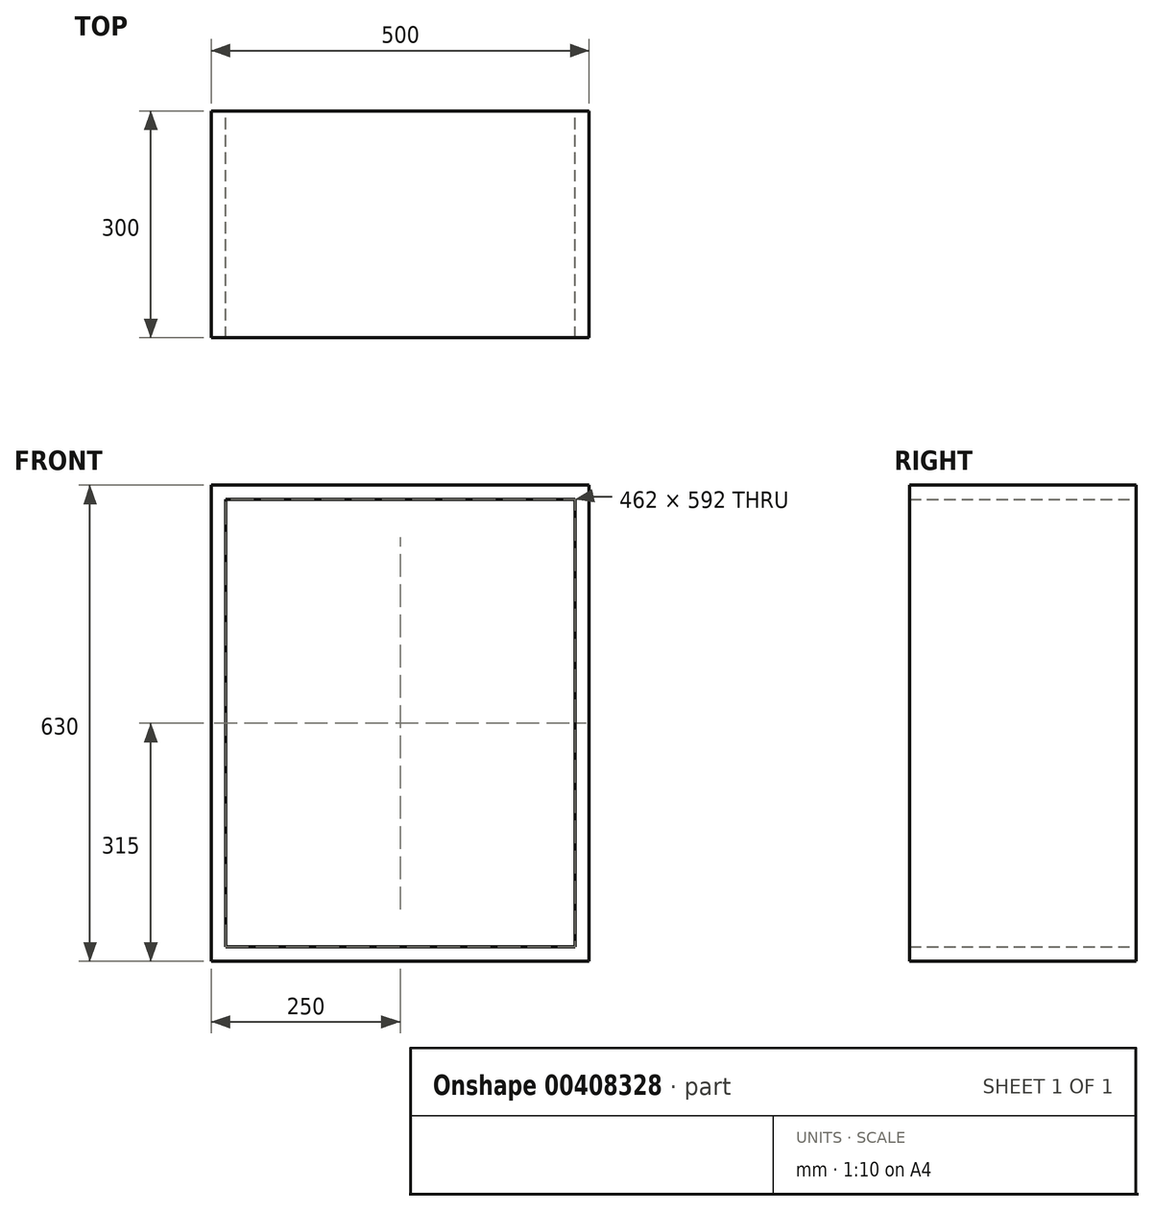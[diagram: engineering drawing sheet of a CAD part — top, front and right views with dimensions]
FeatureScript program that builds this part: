
annotation { "Feature Type Name" : "Feature", "Feature Type Description" : "" }
export const myFeature = defineFeature(function(context is Context, id is Id, definition is map)
    precondition{}
    {
        {
            assignVariable(context, id + "F0", {"name" : "T_Regal", "anyValue" : 300 * mm});
        }
        {
            var Q0;
            Q0=qCreatedBy(makeId("Front.planeOp"),FACE);
            var sketch = newSketch(context, id + "F1", { "sketchPlane" : qUnion([Q0])});
            skLineSegment(sketch, "E0.bottom", {"start": v(-250, 630) * mm, "end": v(250, 630) * mm});
            skLineSegment(sketch, "E0.top", {"start": v(-250, 0) * mm, "end": v(250, 0) * mm});
            skLineSegment(sketch, "E0.left", {"start": v(-250, 630) * mm, "end": v(-250, 0) * mm});
            skLineSegment(sketch, "E0.right", {"start": v(250, 630) * mm, "end": v(250, 0) * mm});
            skLineSegment(sketch, "E1.bottom", {"start": v(-231, 611) * mm, "end": v(231, 611) * mm});
            skLineSegment(sketch, "E1.top", {"start": v(-231, 19) * mm, "end": v(231, 19) * mm});
            skLineSegment(sketch, "E1.left", {"start": v(-231, 611) * mm, "end": v(-231, 19) * mm});
            skLineSegment(sketch, "E1.right", {"start": v(231, 611) * mm, "end": v(231, 19) * mm});
            skSolve(sketch);
        }
        {
            var Q0;
            Q0 = qSketchRegion(id + "F1", true);
            extrude(context, id + "F2", {"entities" : qUnion([Q0]), "depth" : getVariable(context, 'T_Regal')});
        }
    });
